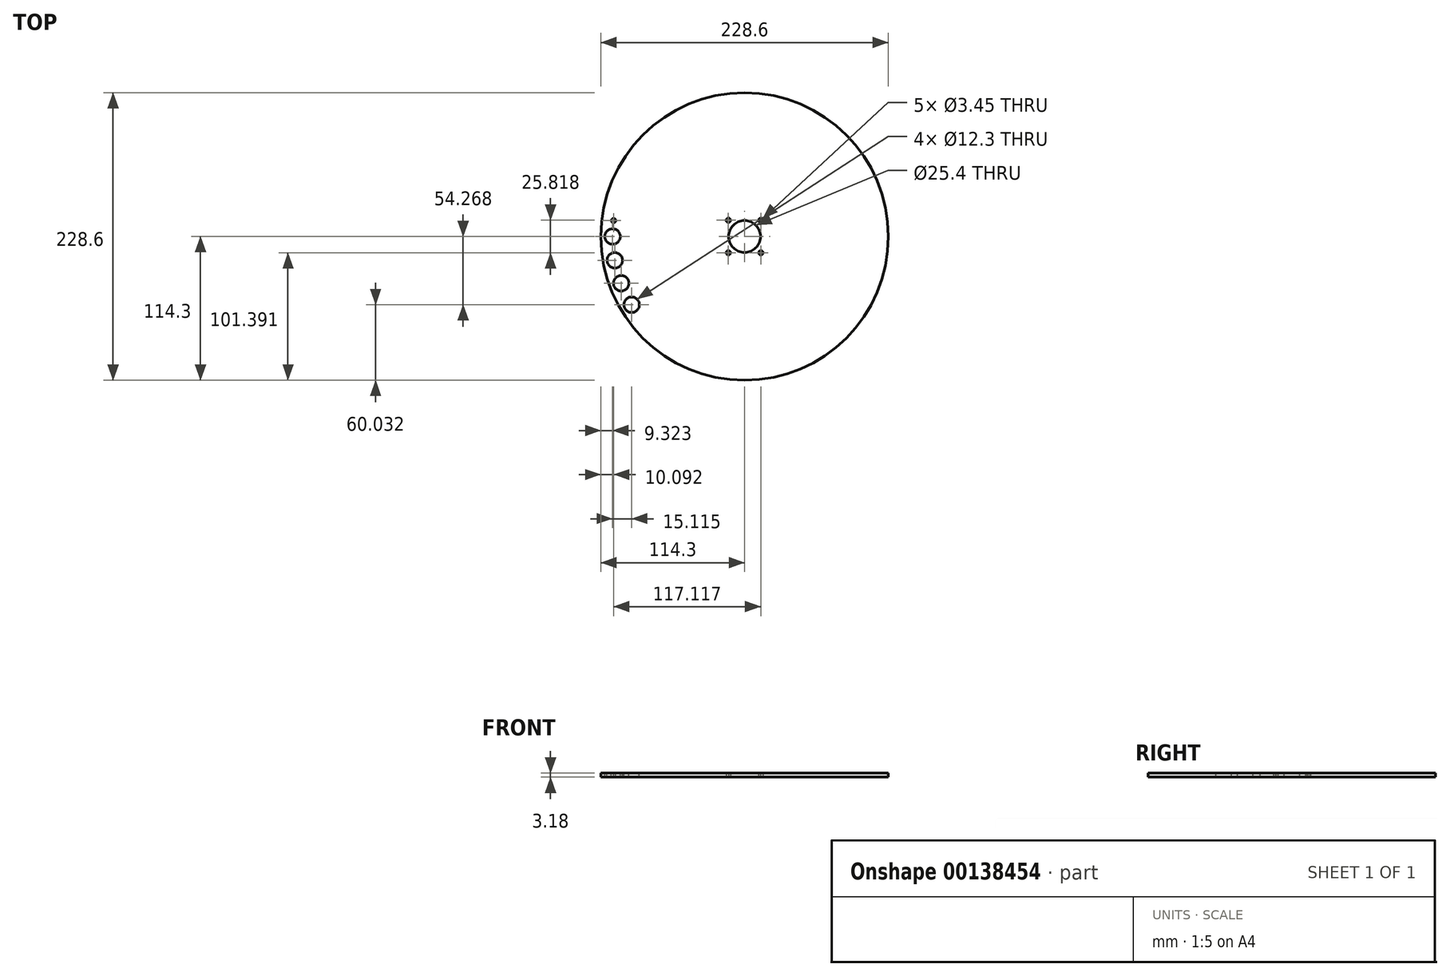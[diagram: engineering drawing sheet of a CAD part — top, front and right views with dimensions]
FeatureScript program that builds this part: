
annotation { "Feature Type Name" : "Feature", "Feature Type Description" : "" }
export const myFeature = defineFeature(function(context is Context, id is Id, definition is map)
    precondition{}
    {
        {
            var Q0;
            Q0=qCreatedBy(makeId("Top.planeOp"),FACE);
            var sketch = newSketch(context, id + "F0", { "sketchPlane" : qUnion([Q0])});
            skCircle(sketch, "E0", {"center": v(0, 0) * mm, "radius": 114.3 * mm});
            skCircle(sketch, "E1", {"center": v(0, 0) * mm, "radius": 12.7 * mm});
            skCircle(sketch, "E2", {"center": v(0, 0) * mm, "radius": 14.29 * mm, "construction": true});
            skLineSegment(sketch, "E3.bottom", {"start": v(-12.9, -12.9) * mm, "end": v(12.9, -12.9) * mm, "construction": true});
            skLineSegment(sketch, "E3.top", {"start": v(-12.9, 12.9) * mm, "end": v(12.9, 12.9) * mm, "construction": true});
            skLineSegment(sketch, "E3.left", {"start": v(-12.9, -12.9) * mm, "end": v(-12.9, 12.9) * mm, "construction": true});
            skLineSegment(sketch, "E3.right", {"start": v(12.9, -12.9) * mm, "end": v(12.9, 12.9) * mm, "construction": true});
            skCircle(sketch, "E4", {"center": v(-12.9, -12.9) * mm, "radius": 3.97 * mm, "construction": true});
            skCircle(sketch, "E5", {"center": v(-12.9, -12.9) * mm, "radius": 1.73 * mm});
            skCircle(sketch, "E6", {"center": v(-12.9, 12.9) * mm, "radius": 1.73 * mm});
            skCircle(sketch, "E7", {"center": v(12.9, 12.9) * mm, "radius": 1.73 * mm});
            skCircle(sketch, "E8", {"center": v(12.9, -12.9) * mm, "radius": 1.73 * mm});
            skSolve(sketch);
        }
        {
            var Q0;
            Q0=qSketchRegion(id+"F0",true);
            extrude(context, id + "F1", {"entities" : qUnion([Q0]), "depth" : 3.17 * mm});
        }
        {
            var Q0;
            Q0=makeQuery(id+"F1.opExtrude","CAP_FACE",FACE,{"disambiguationData":[OSD([sQuery(id+"F0.wireOp",EDGE,"E0"),sQuery(id+"F0.wireOp",EDGE,"E1")])],"isStart":false});
            var sketch = newSketch(context, id + "F2", { "sketchPlane" : qUnion([Q0])});
            skLineSegment(sketch, "E9", {"start": v(0, 0) * mm, "end": v(-104.98, 0) * mm, "construction": true});
            skLineSegment(sketch, "E10", {"start": v(-104.98, 0) * mm, "end": v(-114.3, 0) * mm, "construction": true});
            skCircle(sketch, "E11", {"center": v(-104.98, 0) * mm, "radius": 6.15 * mm});
            skLineSegment(sketch, "E12", {"start": v(0, 0) * mm, "end": v(-103.26, -18.9) * mm, "construction": true});
            skLineSegment(sketch, "E13", {"start": v(0, 0) * mm, "end": v(-98.17, -37.2) * mm, "construction": true});
            skLineSegment(sketch, "E14", {"start": v(0, 0) * mm, "end": v(-89.86, -54.27) * mm, "construction": true});
            skLineSegment(sketch, "E15", {"start": v(0, 0) * mm, "end": v(-104.2, 12.68) * mm, "construction": true});
            skCircle(sketch, "E16", {"center": v(-103.26, -18.9) * mm, "radius": 6.15 * mm});
            skCircle(sketch, "E17", {"center": v(-98.17, -37.2) * mm, "radius": 6.15 * mm});
            skCircle(sketch, "E18", {"center": v(-89.86, -54.27) * mm, "radius": 6.15 * mm});
            skLineSegment(sketch, "E19", {"start": v(-104.98, 0) * mm, "end": v(-103.26, -18.9) * mm, "construction": true});
            skLineSegment(sketch, "E20", {"start": v(-98.17, -37.2) * mm, "end": v(-103.26, -18.9) * mm, "construction": true});
            skLineSegment(sketch, "E21", {"start": v(-98.17, -37.2) * mm, "end": v(-89.86, -54.27) * mm, "construction": true});
            skCircle(sketch, "E22", {"center": v(-104.2, 12.68) * mm, "radius": 1.73 * mm});
            skLineSegment(sketch, "E23", {"start": v(-104.2, 12.68) * mm, "end": v(-104.98, 0) * mm, "construction": true});
            skLineSegment(sketch, "E24", {"start": v(0, 0) * mm, "end": v(-82.65, -64.72) * mm, "construction": true});
            skLineSegment(sketch, "E25", {"start": v(-82.65, -64.72) * mm, "end": v(-89.86, -54.27) * mm, "construction": true});
            skCircle(sketch, "E26", {"center": v(-104.2, 12.68) * mm, "radius": 6.35 * mm, "construction": true});
            skCircle(sketch, "E27", {"center": v(-104.98, 0) * mm, "radius": 6.35 * mm, "construction": true});
            skSolve(sketch);
        }
        {
            var Q0;
            Q0=qSketchRegion(id+"F2",true);
            var Q1;
            Q1=makeQuery(id+"F1.opExtrude","CAP_FACE",FACE,{"disambiguationData":[OSD([sQuery(id+"F0.wireOp",EDGE,"E0"),sQuery(id+"F0.wireOp",EDGE,"E1")])],"isStart":true});
            extrude(context, id + "F3", {"entities" : qUnion([Q0]), "operationType" : NewBodyOperationType.REMOVE, "endBound" : BoundingType.UP_TO_SURFACE, "oppositeDirection" : true, "endBoundEntityFace" : qUnion([Q1]), "depth" : 25.4 * mm});
        }
    });
